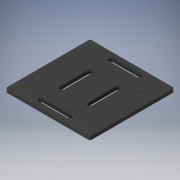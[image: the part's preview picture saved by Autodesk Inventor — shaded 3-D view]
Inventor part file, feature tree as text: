
AUTODESK INVENTOR PART (.ipt)
format: ipt  version: 2017 (Build 210142000, 142)  size: 224,256 bytes
history: native  units: in
note: dims shown in document units (in); Inventor stores cm internally (conversion verified against a paired STEP export)
features: extrude x6, sketch x6, projected_geometry x2, fillet x1
ambient origin geometry x8: Origin, YZ Plane, XZ Plane, XY Plane, X Axis, Y Axis, Z Axis, Center Point
bodies: Solid1 (feature_tree)
feature tree (15):
  extrude  "Extrusion1"  Depth=9.0in
  fillet  "Fillet1"  Radius=3.0in
  extrude  "camMount"  Depth=0.125in
  extrude  "TilitMount"  Depth=0.125in
  extrude  "Extrusion6"  Depth=3.0in
  extrude  "Extrusion7"  Depth=0.125in
  extrude  "Extrusion8"  Depth=0.125in
  sketch  "Sketch1"  dims[d0=9.0in d1=9.0in d2=3.0in]
  sketch  "Sketch4"  dims[d3=1.5in d4=0.125in]
  projected_geometry  "Projected Loop2"
  sketch  "Sketch5"  dims[d5=3.0in d6=0.125in]
  projected_geometry  "Projected Loop3"
  sketch  "Sketch6"  dims[d7=1.5in d8=3.0in]
  sketch  "Sketch7"  dims[d9=0.125in d10=0.125in]
  sketch  "Sketch8"  dims[d11=0.375in d12=0.0in d21=0.125in d22=1.625in d23=0.25in d24=2.25in d25=0.125in d26=0.125in d27=1.0in d28=0.0in d29=0.25in d30=1.465in d31=2.152in d34=1.0in d35=0.0in d36=3.402in d37=1.5in d38=0.125in d39=3.0in d40=7.5in d41=0.5in d42=0.5in d43=3.0in d44=0.5in d45=0.5in d46=1.0in d47=0.0in d48=0.375in d49=0.5in d50=0.125in d51=1.0in d52=0.0in d53=1.5in d54=1.0in d55=0.125in d56=0.125in d57=1.0in d58=0.0in]
